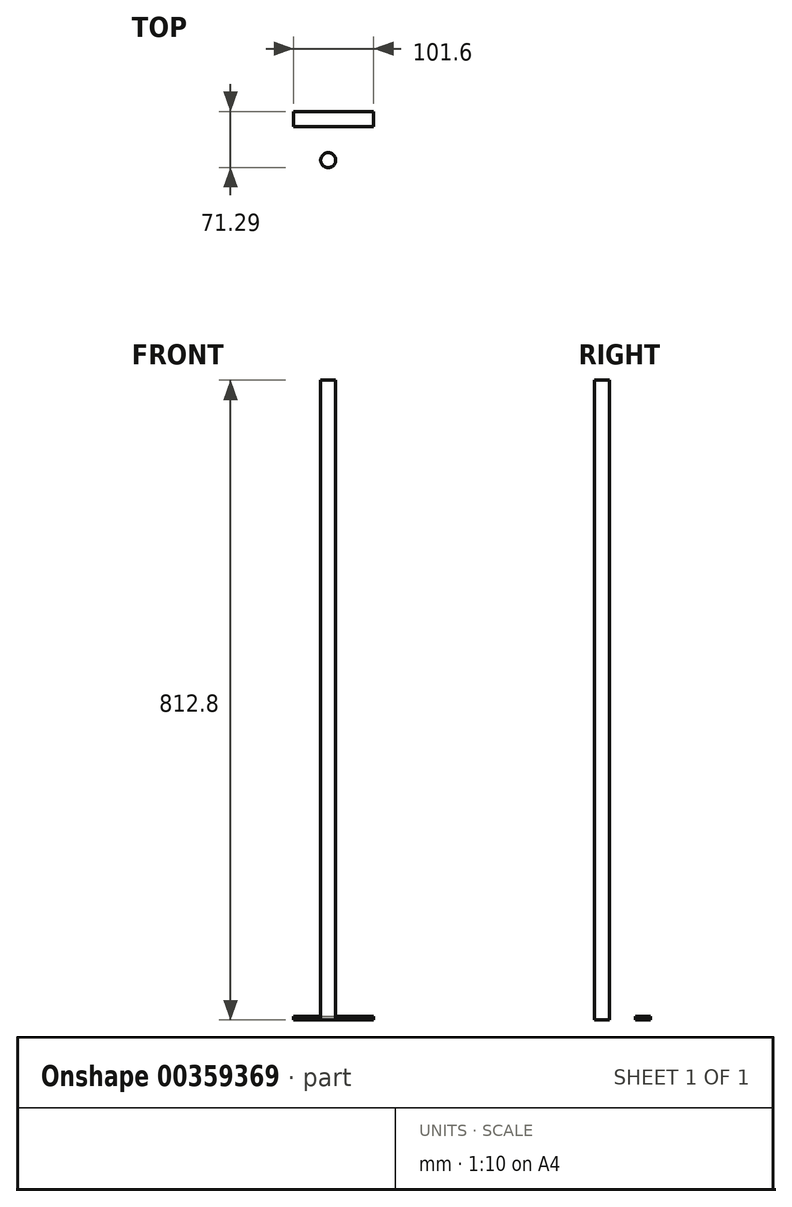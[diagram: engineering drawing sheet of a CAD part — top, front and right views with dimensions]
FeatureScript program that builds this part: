
annotation { "Feature Type Name" : "Feature", "Feature Type Description" : "" }
export const myFeature = defineFeature(function(context is Context, id is Id, definition is map)
    precondition{}
    {
        {
            var Q0;
            Q0=qCreatedBy(makeId("Top.planeOp"),FACE);
            var sketch = newSketch(context, id + "F0", { "sketchPlane" : qUnion([Q0])});
            skCircle(sketch, "E0", {"center": v(0, 0) * mm, "radius": 9.53 * mm});
            skLineSegment(sketch, "E1.bottom", {"start": v(-43.97, 42.71) * mm, "end": v(57.63, 42.71) * mm});
            skLineSegment(sketch, "E1.top", {"start": v(-43.97, 61.76) * mm, "end": v(57.63, 61.76) * mm});
            skLineSegment(sketch, "E1.left", {"start": v(-43.97, 42.71) * mm, "end": v(-43.97, 61.76) * mm});
            skLineSegment(sketch, "E1.right", {"start": v(57.63, 42.71) * mm, "end": v(57.63, 61.76) * mm});
            skSolve(sketch);
        }
        {
            var Q0;
            Q0=makeQuery(id+"F0.imprint","IMPRINT",FACE,{"disambiguationData":[TD([[makeQuery(id+"F0.imprint","IMPRINT",EDGE,{"derivedFrom":sQuery(id+"F0.wireOp",EDGE,"E0")}),1.0]])]});
            extrude(context, id + "F1", {"entities" : qUnion([Q0]), "depth" : 812.8 * mm, "offsetDistance" : 25.4 * mm});
        }
        {
            var Q0;
            Q0=makeQuery(id+"F0.imprint","IMPRINT",FACE,{"disambiguationData":[TD([[makeQuery(id+"F0.imprint","IMPRINT",EDGE,{"derivedFrom":sQuery(id+"F0.wireOp",EDGE,"E1.bottom")}),1.0]])]});
            extrude(context, id + "F2", {"entities" : qUnion([Q0]), "depth" : 4.76 * mm, "offsetDistance" : 25.4 * mm});
        }
    });
